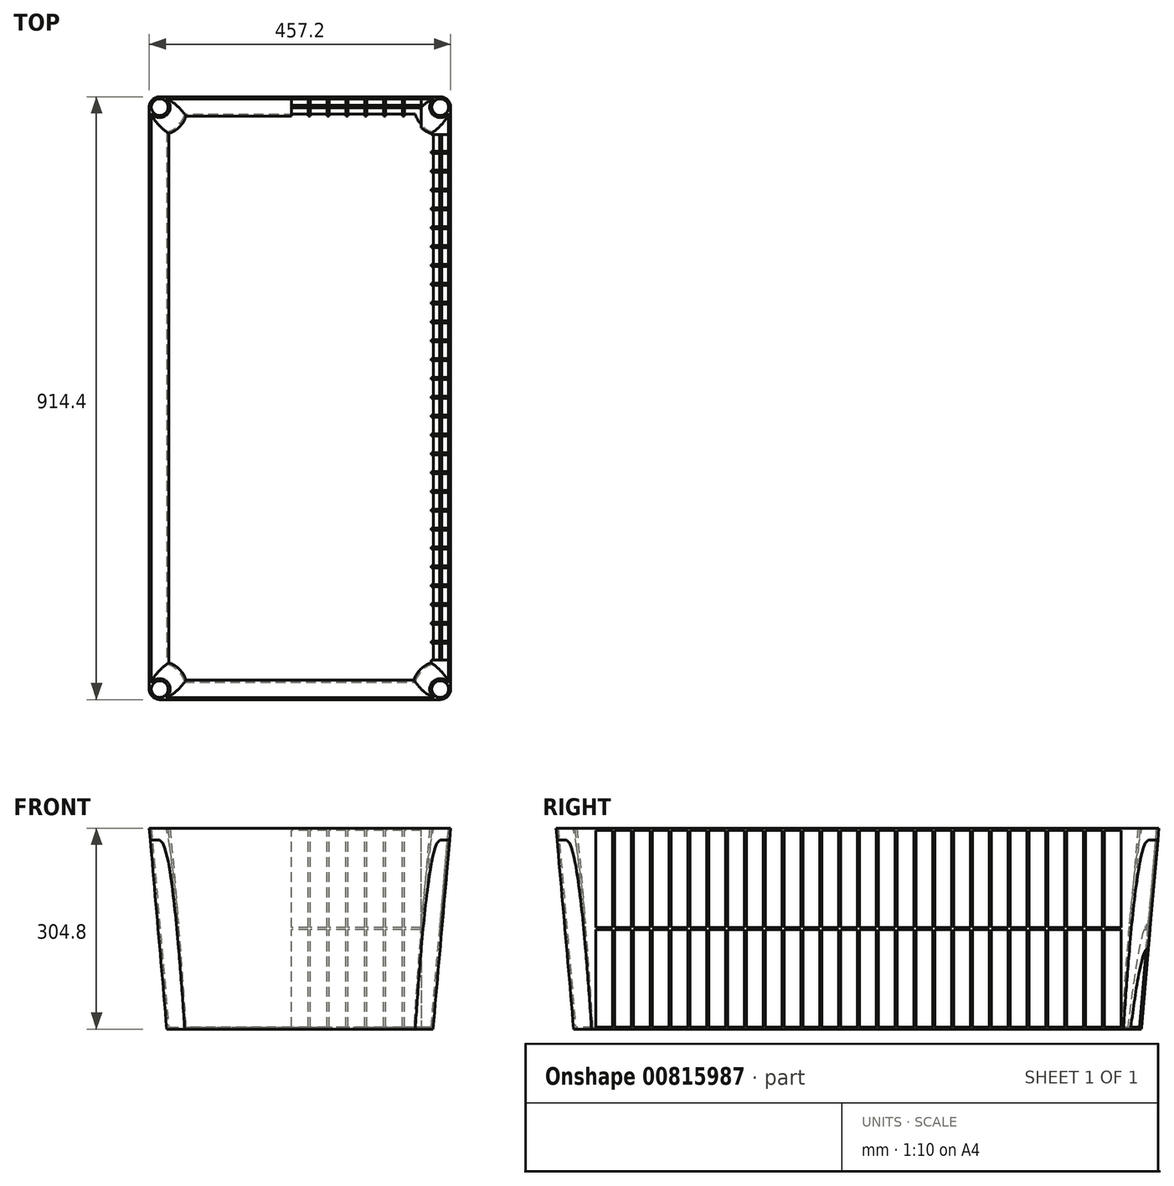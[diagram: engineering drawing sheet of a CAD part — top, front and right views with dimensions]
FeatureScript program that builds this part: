
annotation { "Feature Type Name" : "Feature", "Feature Type Description" : "" }
export const myFeature = defineFeature(function(context is Context, id is Id, definition is map)
    precondition{}
    {
        {
            var Q0;
            Q0=qCreatedBy(makeId("Right.planeOp"),FACE);
            cPlane(context, id + "F0", {"entities" : qUnion([Q0]), "cplaneType" : CPlaneType.OFFSET, "offset" : 0 * mm, "width" : 152.4 * mm, "height" : 152.4 * mm});
        }
        {
            var Q0;
            Q0=qCreatedBy(makeId("Top.planeOp"),FACE);
            var sketch = newSketch(context, id + "F1", { "sketchPlane" : qUnion([Q0])});
            skLineSegment(sketch, "E0.bottom", {"start": v(-212.73, 457.2) * mm, "end": v(212.72, 457.2) * mm});
            skLineSegment(sketch, "E0.top", {"start": v(-212.73, -457.2) * mm, "end": v(212.73, -457.2) * mm});
            skLineSegment(sketch, "E0.left", {"start": v(-228.6, 441.32) * mm, "end": v(-228.6, -441.33) * mm});
            skLineSegment(sketch, "E0.right", {"start": v(228.6, 441.33) * mm, "end": v(228.6, -441.33) * mm});
            skLineSegment(sketch, "E1", {"start": v(-228.6, 457.2) * mm, "end": v(228.6, -457.2) * mm, "construction": true});
            skPoint(sketch, "E2.visualSharp", {"position": v(-228.6, -457.2) * mm});
            skArc(sketch, "E2.filletArc", {"start": v(-228.6, -441.33) * mm, "mid": v(-223.95, -452.55) * mm, "end": v(-212.73, -457.2) * mm});
            skPoint(sketch, "E3.visualSharp", {"position": v(-228.6, 457.2) * mm});
            skArc(sketch, "E3.filletArc", {"start": v(-212.73, 457.2) * mm, "mid": v(-223.95, 452.55) * mm, "end": v(-228.6, 441.32) * mm});
            skPoint(sketch, "E4.visualSharp", {"position": v(228.6, 457.2) * mm});
            skArc(sketch, "E4.filletArc", {"start": v(228.6, 441.33) * mm, "mid": v(223.95, 452.55) * mm, "end": v(212.72, 457.2) * mm});
            skPoint(sketch, "E5.visualSharp", {"position": v(228.6, -457.2) * mm});
            skArc(sketch, "E5.filletArc", {"start": v(212.73, -457.2) * mm, "mid": v(223.95, -452.55) * mm, "end": v(228.6, -441.33) * mm});
            skCircle(sketch, "E6", {"center": v(-212.73, -441.33) * mm, "radius": 12.7 * mm});
            skCircle(sketch, "E7", {"center": v(212.73, -441.33) * mm, "radius": 12.7 * mm});
            skCircle(sketch, "E8", {"center": v(-212.73, 441.32) * mm, "radius": 12.7 * mm});
            skCircle(sketch, "E9", {"center": v(212.72, 441.33) * mm, "radius": 12.7 * mm});
            skSolve(sketch);
        }
        {
            var Q0;
            Q0=makeQuery(id+"F1.imprint","IMPRINT",FACE,{"disambiguationData":[TD([[makeQuery(id+"F1.imprint","IMPRINT",EDGE,{"derivedFrom":sQuery(id+"F1.wireOp",EDGE,"E0.bottom")}),-1.0]])]});
            extrude(context, id + "F2", {"entities" : qUnion([Q0]), "oppositeDirection" : true, "depth" : 304.8 * mm, "offsetDistance" : 25.4 * mm, "hasDraft" : true, "draftAngle" : 5 * degree, "draftPullDirection" : true});
        }
        {
            var Q0;
            Q0=makeQuery(id+"F2.opExtrude","CAP_FACE",FACE,{"disambiguationData":[OSD([sQuery(id+"F1.wireOp",EDGE,"E0.bottom"),sQuery(id+"F1.wireOp",EDGE,"E0.top"),sQuery(id+"F1.wireOp",EDGE,"E0.left"),sQuery(id+"F1.wireOp",EDGE,"E0.right"),sQuery(id+"F1.wireOp",EDGE,"E2.filletArc"),sQuery(id+"F1.wireOp",EDGE,"E3.filletArc"),sQuery(id+"F1.wireOp",EDGE,"E4.filletArc"),sQuery(id+"F1.wireOp",EDGE,"E5.filletArc"),sQuery(id+"F1.wireOp",EDGE,"E6"),sQuery(id+"F1.wireOp",EDGE,"E7"),sQuery(id+"F1.wireOp",EDGE,"E8"),sQuery(id+"F1.wireOp",EDGE,"E9")])],"isStart":true});
            shell(context, id + "F3", {"entities" : qUnion([Q0]), "thickness" : 3.17 * mm});
        }
        {
            var Q0;
            Q0=qCreatedBy(id+"F0.planeOp",FACE);
            var sketch = newSketch(context, id + "F4", { "sketchPlane" : qUnion([Q0])});
            skLineSegment(sketch, "E10.bottom", {"start": v(-396.88, -3.18) * mm, "end": v(-371.48, -3.18) * mm});
            skLineSegment(sketch, "E10.top", {"start": v(-396.88, -150.81) * mm, "end": v(-371.48, -150.81) * mm});
            skLineSegment(sketch, "E10.left", {"start": v(-396.88, -3.17) * mm, "end": v(-396.88, -150.81) * mm});
            skLineSegment(sketch, "E10.right", {"start": v(-371.48, -3.18) * mm, "end": v(-371.48, -150.81) * mm});
            skLineSegment(sketch, "E11.0.1.0", {"start": v(-371.48, -153.99) * mm, "end": v(-371.48, -301.62) * mm});
            skLineSegment(sketch, "E11.0.1.1", {"start": v(-396.88, -153.99) * mm, "end": v(-396.88, -301.63) * mm});
            skLineSegment(sketch, "E11.0.1.2", {"start": v(-396.88, -153.99) * mm, "end": v(-371.48, -153.99) * mm});
            skLineSegment(sketch, "E11.0.1.3", {"start": v(-396.88, -301.62) * mm, "end": v(-371.48, -301.62) * mm});
            skLineSegment(sketch, "E11.1.0.0", {"start": v(-342.9, -3.18) * mm, "end": v(-342.9, -150.81) * mm});
            skLineSegment(sketch, "E11.1.0.1", {"start": v(-368.3, -3.17) * mm, "end": v(-368.3, -150.81) * mm});
            skLineSegment(sketch, "E11.1.0.2", {"start": v(-368.3, -3.18) * mm, "end": v(-342.9, -3.18) * mm});
            skLineSegment(sketch, "E11.1.0.3", {"start": v(-368.3, -150.81) * mm, "end": v(-342.9, -150.81) * mm});
            skLineSegment(sketch, "E11.1.1.0", {"start": v(-342.9, -153.99) * mm, "end": v(-342.9, -301.62) * mm});
            skLineSegment(sketch, "E11.1.1.1", {"start": v(-368.3, -153.99) * mm, "end": v(-368.3, -301.63) * mm});
            skLineSegment(sketch, "E11.1.1.2", {"start": v(-368.3, -153.99) * mm, "end": v(-342.9, -153.99) * mm});
            skLineSegment(sketch, "E11.1.1.3", {"start": v(-368.3, -301.63) * mm, "end": v(-342.9, -301.63) * mm});
            skLineSegment(sketch, "E11.2.0.0", {"start": v(-314.33, -3.18) * mm, "end": v(-314.33, -150.81) * mm});
            skLineSegment(sketch, "E11.2.0.1", {"start": v(-339.73, -3.17) * mm, "end": v(-339.73, -150.81) * mm});
            skLineSegment(sketch, "E11.2.0.2", {"start": v(-339.73, -3.18) * mm, "end": v(-314.33, -3.18) * mm});
            skLineSegment(sketch, "E11.2.0.3", {"start": v(-339.72, -150.81) * mm, "end": v(-314.32, -150.81) * mm});
            skLineSegment(sketch, "E11.2.1.0", {"start": v(-314.33, -153.99) * mm, "end": v(-314.33, -301.62) * mm});
            skLineSegment(sketch, "E11.2.1.1", {"start": v(-339.73, -153.99) * mm, "end": v(-339.73, -301.63) * mm});
            skLineSegment(sketch, "E11.2.1.2", {"start": v(-339.73, -153.99) * mm, "end": v(-314.33, -153.99) * mm});
            skLineSegment(sketch, "E11.2.1.3", {"start": v(-339.72, -301.63) * mm, "end": v(-314.32, -301.63) * mm});
            skLineSegment(sketch, "E11.3.0.0", {"start": v(-285.75, -3.18) * mm, "end": v(-285.75, -150.81) * mm});
            skLineSegment(sketch, "E11.3.0.1", {"start": v(-311.15, -3.17) * mm, "end": v(-311.15, -150.81) * mm});
            skLineSegment(sketch, "E11.3.0.2", {"start": v(-311.15, -3.18) * mm, "end": v(-285.75, -3.18) * mm});
            skLineSegment(sketch, "E11.3.0.3", {"start": v(-311.15, -150.81) * mm, "end": v(-285.75, -150.81) * mm});
            skLineSegment(sketch, "E11.3.1.0", {"start": v(-285.75, -153.99) * mm, "end": v(-285.75, -301.62) * mm});
            skLineSegment(sketch, "E11.3.1.1", {"start": v(-311.15, -153.99) * mm, "end": v(-311.15, -301.63) * mm});
            skLineSegment(sketch, "E11.3.1.2", {"start": v(-311.15, -153.99) * mm, "end": v(-285.75, -153.99) * mm});
            skLineSegment(sketch, "E11.3.1.3", {"start": v(-311.15, -301.63) * mm, "end": v(-285.75, -301.63) * mm});
            skLineSegment(sketch, "E11.4.0.0", {"start": v(-257.18, -3.18) * mm, "end": v(-257.18, -150.81) * mm});
            skLineSegment(sketch, "E11.4.0.1", {"start": v(-282.57, -3.17) * mm, "end": v(-282.57, -150.81) * mm});
            skLineSegment(sketch, "E11.4.0.2", {"start": v(-282.57, -3.18) * mm, "end": v(-257.18, -3.18) * mm});
            skLineSegment(sketch, "E11.4.0.3", {"start": v(-282.57, -150.81) * mm, "end": v(-257.17, -150.81) * mm});
            skLineSegment(sketch, "E11.4.1.0", {"start": v(-257.18, -153.99) * mm, "end": v(-257.18, -301.62) * mm});
            skLineSegment(sketch, "E11.4.1.1", {"start": v(-282.57, -153.99) * mm, "end": v(-282.57, -301.63) * mm});
            skLineSegment(sketch, "E11.4.1.2", {"start": v(-282.57, -153.99) * mm, "end": v(-257.18, -153.99) * mm});
            skLineSegment(sketch, "E11.4.1.3", {"start": v(-282.57, -301.63) * mm, "end": v(-257.17, -301.63) * mm});
            skLineSegment(sketch, "E11.5.0.0", {"start": v(-228.6, -3.18) * mm, "end": v(-228.6, -150.81) * mm});
            skLineSegment(sketch, "E11.5.0.1", {"start": v(-254, -3.17) * mm, "end": v(-254, -150.81) * mm});
            skLineSegment(sketch, "E11.5.0.2", {"start": v(-254, -3.18) * mm, "end": v(-228.6, -3.18) * mm});
            skLineSegment(sketch, "E11.5.0.3", {"start": v(-254, -150.81) * mm, "end": v(-228.6, -150.81) * mm});
            skLineSegment(sketch, "E11.5.1.0", {"start": v(-228.6, -153.99) * mm, "end": v(-228.6, -301.62) * mm});
            skLineSegment(sketch, "E11.5.1.1", {"start": v(-254, -153.99) * mm, "end": v(-254, -301.63) * mm});
            skLineSegment(sketch, "E11.5.1.2", {"start": v(-254, -153.99) * mm, "end": v(-228.6, -153.99) * mm});
            skLineSegment(sketch, "E11.5.1.3", {"start": v(-254, -301.63) * mm, "end": v(-228.6, -301.63) * mm});
            skLineSegment(sketch, "E11.6.0.0", {"start": v(-200.02, -3.18) * mm, "end": v(-200.02, -150.81) * mm});
            skLineSegment(sketch, "E11.6.0.1", {"start": v(-225.42, -3.17) * mm, "end": v(-225.42, -150.81) * mm});
            skLineSegment(sketch, "E11.6.0.2", {"start": v(-225.42, -3.18) * mm, "end": v(-200.02, -3.18) * mm});
            skLineSegment(sketch, "E11.6.0.3", {"start": v(-225.42, -150.81) * mm, "end": v(-200.02, -150.81) * mm});
            skLineSegment(sketch, "E11.6.1.0", {"start": v(-200.02, -153.99) * mm, "end": v(-200.02, -301.62) * mm});
            skLineSegment(sketch, "E11.6.1.1", {"start": v(-225.42, -153.99) * mm, "end": v(-225.42, -301.63) * mm});
            skLineSegment(sketch, "E11.6.1.2", {"start": v(-225.42, -153.99) * mm, "end": v(-200.02, -153.99) * mm});
            skLineSegment(sketch, "E11.6.1.3", {"start": v(-225.42, -301.63) * mm, "end": v(-200.02, -301.63) * mm});
            skLineSegment(sketch, "E11.7.0.0", {"start": v(-171.45, -3.18) * mm, "end": v(-171.45, -150.81) * mm});
            skLineSegment(sketch, "E11.7.0.1", {"start": v(-196.85, -3.17) * mm, "end": v(-196.85, -150.81) * mm});
            skLineSegment(sketch, "E11.7.0.2", {"start": v(-196.85, -3.18) * mm, "end": v(-171.45, -3.18) * mm});
            skLineSegment(sketch, "E11.7.0.3", {"start": v(-196.85, -150.81) * mm, "end": v(-171.45, -150.81) * mm});
            skLineSegment(sketch, "E11.7.1.0", {"start": v(-171.45, -153.99) * mm, "end": v(-171.45, -301.62) * mm});
            skLineSegment(sketch, "E11.7.1.1", {"start": v(-196.85, -153.99) * mm, "end": v(-196.85, -301.63) * mm});
            skLineSegment(sketch, "E11.7.1.2", {"start": v(-196.85, -153.99) * mm, "end": v(-171.45, -153.99) * mm});
            skLineSegment(sketch, "E11.7.1.3", {"start": v(-196.85, -301.63) * mm, "end": v(-171.45, -301.63) * mm});
            skLineSegment(sketch, "E11.8.0.0", {"start": v(-142.87, -3.18) * mm, "end": v(-142.87, -150.81) * mm});
            skLineSegment(sketch, "E11.8.0.1", {"start": v(-168.27, -3.17) * mm, "end": v(-168.27, -150.81) * mm});
            skLineSegment(sketch, "E11.8.0.2", {"start": v(-168.27, -3.18) * mm, "end": v(-142.87, -3.18) * mm});
            skLineSegment(sketch, "E11.8.0.3", {"start": v(-168.27, -150.81) * mm, "end": v(-142.87, -150.81) * mm});
            skLineSegment(sketch, "E11.8.1.0", {"start": v(-142.87, -153.99) * mm, "end": v(-142.87, -301.62) * mm});
            skLineSegment(sketch, "E11.8.1.1", {"start": v(-168.27, -153.99) * mm, "end": v(-168.27, -301.63) * mm});
            skLineSegment(sketch, "E11.8.1.2", {"start": v(-168.27, -153.99) * mm, "end": v(-142.87, -153.99) * mm});
            skLineSegment(sketch, "E11.8.1.3", {"start": v(-168.27, -301.63) * mm, "end": v(-142.87, -301.63) * mm});
            skLineSegment(sketch, "E11.9.0.0", {"start": v(-114.3, -3.18) * mm, "end": v(-114.3, -150.81) * mm});
            skLineSegment(sketch, "E11.9.0.1", {"start": v(-139.7, -3.17) * mm, "end": v(-139.7, -150.81) * mm});
            skLineSegment(sketch, "E11.9.0.2", {"start": v(-139.7, -3.18) * mm, "end": v(-114.3, -3.18) * mm});
            skLineSegment(sketch, "E11.9.0.3", {"start": v(-139.7, -150.81) * mm, "end": v(-114.3, -150.81) * mm});
            skLineSegment(sketch, "E11.9.1.0", {"start": v(-114.3, -153.99) * mm, "end": v(-114.3, -301.62) * mm});
            skLineSegment(sketch, "E11.9.1.1", {"start": v(-139.7, -153.99) * mm, "end": v(-139.7, -301.63) * mm});
            skLineSegment(sketch, "E11.9.1.2", {"start": v(-139.7, -153.99) * mm, "end": v(-114.3, -153.99) * mm});
            skLineSegment(sketch, "E11.9.1.3", {"start": v(-139.7, -301.63) * mm, "end": v(-114.3, -301.63) * mm});
            skLineSegment(sketch, "E11.10.0.0", {"start": v(-85.72, -3.18) * mm, "end": v(-85.72, -150.81) * mm});
            skLineSegment(sketch, "E11.10.0.1", {"start": v(-111.12, -3.17) * mm, "end": v(-111.12, -150.81) * mm});
            skLineSegment(sketch, "E11.10.0.2", {"start": v(-111.12, -3.18) * mm, "end": v(-85.72, -3.18) * mm});
            skLineSegment(sketch, "E11.10.0.3", {"start": v(-111.12, -150.81) * mm, "end": v(-85.72, -150.81) * mm});
            skLineSegment(sketch, "E11.10.1.0", {"start": v(-85.72, -153.99) * mm, "end": v(-85.72, -301.62) * mm});
            skLineSegment(sketch, "E11.10.1.1", {"start": v(-111.12, -153.99) * mm, "end": v(-111.12, -301.63) * mm});
            skLineSegment(sketch, "E11.10.1.2", {"start": v(-111.12, -153.99) * mm, "end": v(-85.72, -153.99) * mm});
            skLineSegment(sketch, "E11.10.1.3", {"start": v(-111.12, -301.63) * mm, "end": v(-85.72, -301.63) * mm});
            skLineSegment(sketch, "E11.11.0.0", {"start": v(-57.15, -3.18) * mm, "end": v(-57.15, -150.81) * mm});
            skLineSegment(sketch, "E11.11.0.1", {"start": v(-82.55, -3.17) * mm, "end": v(-82.55, -150.81) * mm});
            skLineSegment(sketch, "E11.11.0.2", {"start": v(-82.55, -3.18) * mm, "end": v(-57.15, -3.18) * mm});
            skLineSegment(sketch, "E11.11.0.3", {"start": v(-82.55, -150.81) * mm, "end": v(-57.15, -150.81) * mm});
            skLineSegment(sketch, "E11.11.1.0", {"start": v(-57.15, -153.99) * mm, "end": v(-57.15, -301.62) * mm});
            skLineSegment(sketch, "E11.11.1.1", {"start": v(-82.55, -153.99) * mm, "end": v(-82.55, -301.63) * mm});
            skLineSegment(sketch, "E11.11.1.2", {"start": v(-82.55, -153.99) * mm, "end": v(-57.15, -153.99) * mm});
            skLineSegment(sketch, "E11.11.1.3", {"start": v(-82.55, -301.63) * mm, "end": v(-57.15, -301.63) * mm});
            skLineSegment(sketch, "E11.12.0.0", {"start": v(-28.57, -3.18) * mm, "end": v(-28.57, -150.81) * mm});
            skLineSegment(sketch, "E11.12.0.1", {"start": v(-53.97, -3.17) * mm, "end": v(-53.97, -150.81) * mm});
            skLineSegment(sketch, "E11.12.0.2", {"start": v(-53.97, -3.18) * mm, "end": v(-28.57, -3.18) * mm});
            skLineSegment(sketch, "E11.12.0.3", {"start": v(-53.97, -150.81) * mm, "end": v(-28.57, -150.81) * mm});
            skLineSegment(sketch, "E11.12.1.0", {"start": v(-28.57, -153.99) * mm, "end": v(-28.57, -301.62) * mm});
            skLineSegment(sketch, "E11.12.1.1", {"start": v(-53.97, -153.99) * mm, "end": v(-53.97, -301.63) * mm});
            skLineSegment(sketch, "E11.12.1.2", {"start": v(-53.97, -153.99) * mm, "end": v(-28.57, -153.99) * mm});
            skLineSegment(sketch, "E11.12.1.3", {"start": v(-53.97, -301.63) * mm, "end": v(-28.57, -301.63) * mm});
            skLineSegment(sketch, "E11.13.0.0", {"start": v(0, -3.18) * mm, "end": v(0, -150.81) * mm});
            skLineSegment(sketch, "E11.13.0.1", {"start": v(-25.4, -3.17) * mm, "end": v(-25.4, -150.81) * mm});
            skLineSegment(sketch, "E11.13.0.2", {"start": v(-25.4, -3.18) * mm, "end": v(0, -3.18) * mm});
            skLineSegment(sketch, "E11.13.0.3", {"start": v(-25.4, -150.81) * mm, "end": v(0, -150.81) * mm});
            skLineSegment(sketch, "E11.13.1.0", {"start": v(0, -153.99) * mm, "end": v(0, -301.62) * mm});
            skLineSegment(sketch, "E11.13.1.1", {"start": v(-25.4, -153.99) * mm, "end": v(-25.4, -301.63) * mm});
            skLineSegment(sketch, "E11.13.1.2", {"start": v(-25.4, -153.99) * mm, "end": v(0, -153.99) * mm});
            skLineSegment(sketch, "E11.13.1.3", {"start": v(-25.4, -301.63) * mm, "end": v(0, -301.63) * mm});
            skLineSegment(sketch, "E11.14.0.0", {"start": v(28.58, -3.18) * mm, "end": v(28.58, -150.81) * mm});
            skLineSegment(sketch, "E11.14.0.1", {"start": v(3.18, -3.17) * mm, "end": v(3.18, -150.81) * mm});
            skLineSegment(sketch, "E11.14.0.2", {"start": v(3.18, -3.18) * mm, "end": v(28.58, -3.18) * mm});
            skLineSegment(sketch, "E11.14.0.3", {"start": v(3.18, -150.81) * mm, "end": v(28.58, -150.81) * mm});
            skLineSegment(sketch, "E11.14.1.0", {"start": v(28.58, -153.99) * mm, "end": v(28.58, -301.62) * mm});
            skLineSegment(sketch, "E11.14.1.1", {"start": v(3.18, -153.99) * mm, "end": v(3.18, -301.63) * mm});
            skLineSegment(sketch, "E11.14.1.2", {"start": v(3.18, -153.99) * mm, "end": v(28.58, -153.99) * mm});
            skLineSegment(sketch, "E11.14.1.3", {"start": v(3.18, -301.63) * mm, "end": v(28.58, -301.63) * mm});
            skLineSegment(sketch, "E11.15.0.0", {"start": v(57.15, -3.18) * mm, "end": v(57.15, -150.81) * mm});
            skLineSegment(sketch, "E11.15.0.1", {"start": v(31.75, -3.17) * mm, "end": v(31.75, -150.81) * mm});
            skLineSegment(sketch, "E11.15.0.2", {"start": v(31.75, -3.18) * mm, "end": v(57.15, -3.18) * mm});
            skLineSegment(sketch, "E11.15.0.3", {"start": v(31.75, -150.81) * mm, "end": v(57.15, -150.81) * mm});
            skLineSegment(sketch, "E11.15.1.0", {"start": v(57.15, -153.99) * mm, "end": v(57.15, -301.62) * mm});
            skLineSegment(sketch, "E11.15.1.1", {"start": v(31.75, -153.99) * mm, "end": v(31.75, -301.63) * mm});
            skLineSegment(sketch, "E11.15.1.2", {"start": v(31.75, -153.99) * mm, "end": v(57.15, -153.99) * mm});
            skLineSegment(sketch, "E11.15.1.3", {"start": v(31.75, -301.63) * mm, "end": v(57.15, -301.63) * mm});
            skLineSegment(sketch, "E11.16.0.0", {"start": v(85.73, -3.18) * mm, "end": v(85.73, -150.81) * mm});
            skLineSegment(sketch, "E11.16.0.1", {"start": v(60.33, -3.17) * mm, "end": v(60.33, -150.81) * mm});
            skLineSegment(sketch, "E11.16.0.2", {"start": v(60.33, -3.18) * mm, "end": v(85.73, -3.18) * mm});
            skLineSegment(sketch, "E11.16.0.3", {"start": v(60.33, -150.81) * mm, "end": v(85.73, -150.81) * mm});
            skLineSegment(sketch, "E11.16.1.0", {"start": v(85.73, -153.99) * mm, "end": v(85.73, -301.62) * mm});
            skLineSegment(sketch, "E11.16.1.1", {"start": v(60.33, -153.99) * mm, "end": v(60.33, -301.63) * mm});
            skLineSegment(sketch, "E11.16.1.2", {"start": v(60.33, -153.99) * mm, "end": v(85.73, -153.99) * mm});
            skLineSegment(sketch, "E11.16.1.3", {"start": v(60.33, -301.63) * mm, "end": v(85.73, -301.63) * mm});
            skLineSegment(sketch, "E11.17.0.0", {"start": v(114.3, -3.18) * mm, "end": v(114.3, -150.81) * mm});
            skLineSegment(sketch, "E11.17.0.1", {"start": v(88.9, -3.17) * mm, "end": v(88.9, -150.81) * mm});
            skLineSegment(sketch, "E11.17.0.2", {"start": v(88.9, -3.18) * mm, "end": v(114.3, -3.18) * mm});
            skLineSegment(sketch, "E11.17.0.3", {"start": v(88.9, -150.81) * mm, "end": v(114.3, -150.81) * mm});
            skLineSegment(sketch, "E11.17.1.0", {"start": v(114.3, -153.99) * mm, "end": v(114.3, -301.62) * mm});
            skLineSegment(sketch, "E11.17.1.1", {"start": v(88.9, -153.99) * mm, "end": v(88.9, -301.63) * mm});
            skLineSegment(sketch, "E11.17.1.2", {"start": v(88.9, -153.99) * mm, "end": v(114.3, -153.99) * mm});
            skLineSegment(sketch, "E11.17.1.3", {"start": v(88.9, -301.63) * mm, "end": v(114.3, -301.63) * mm});
            skLineSegment(sketch, "E11.18.0.0", {"start": v(142.88, -3.18) * mm, "end": v(142.88, -150.81) * mm});
            skLineSegment(sketch, "E11.18.0.1", {"start": v(117.48, -3.17) * mm, "end": v(117.48, -150.81) * mm});
            skLineSegment(sketch, "E11.18.0.2", {"start": v(117.48, -3.18) * mm, "end": v(142.88, -3.18) * mm});
            skLineSegment(sketch, "E11.18.0.3", {"start": v(117.48, -150.81) * mm, "end": v(142.88, -150.81) * mm});
            skLineSegment(sketch, "E11.18.1.0", {"start": v(142.88, -153.99) * mm, "end": v(142.88, -301.62) * mm});
            skLineSegment(sketch, "E11.18.1.1", {"start": v(117.48, -153.99) * mm, "end": v(117.48, -301.63) * mm});
            skLineSegment(sketch, "E11.18.1.2", {"start": v(117.48, -153.99) * mm, "end": v(142.88, -153.99) * mm});
            skLineSegment(sketch, "E11.18.1.3", {"start": v(117.48, -301.63) * mm, "end": v(142.88, -301.63) * mm});
            skLineSegment(sketch, "E11.19.0.0", {"start": v(171.45, -3.18) * mm, "end": v(171.45, -150.81) * mm});
            skLineSegment(sketch, "E11.19.0.1", {"start": v(146.05, -3.17) * mm, "end": v(146.05, -150.81) * mm});
            skLineSegment(sketch, "E11.19.0.2", {"start": v(146.05, -3.18) * mm, "end": v(171.45, -3.18) * mm});
            skLineSegment(sketch, "E11.19.0.3", {"start": v(146.05, -150.81) * mm, "end": v(171.45, -150.81) * mm});
            skLineSegment(sketch, "E11.19.1.0", {"start": v(171.45, -153.99) * mm, "end": v(171.45, -301.62) * mm});
            skLineSegment(sketch, "E11.19.1.1", {"start": v(146.05, -153.99) * mm, "end": v(146.05, -301.63) * mm});
            skLineSegment(sketch, "E11.19.1.2", {"start": v(146.05, -153.99) * mm, "end": v(171.45, -153.99) * mm});
            skLineSegment(sketch, "E11.19.1.3", {"start": v(146.05, -301.63) * mm, "end": v(171.45, -301.63) * mm});
            skLineSegment(sketch, "E11.20.0.0", {"start": v(200.03, -3.18) * mm, "end": v(200.03, -150.81) * mm});
            skLineSegment(sketch, "E11.20.0.1", {"start": v(174.63, -3.17) * mm, "end": v(174.63, -150.81) * mm});
            skLineSegment(sketch, "E11.20.0.2", {"start": v(174.63, -3.18) * mm, "end": v(200.03, -3.18) * mm});
            skLineSegment(sketch, "E11.20.0.3", {"start": v(174.63, -150.81) * mm, "end": v(200.03, -150.81) * mm});
            skLineSegment(sketch, "E11.20.1.0", {"start": v(200.03, -153.99) * mm, "end": v(200.03, -301.62) * mm});
            skLineSegment(sketch, "E11.20.1.1", {"start": v(174.63, -153.99) * mm, "end": v(174.63, -301.63) * mm});
            skLineSegment(sketch, "E11.20.1.2", {"start": v(174.63, -153.99) * mm, "end": v(200.03, -153.99) * mm});
            skLineSegment(sketch, "E11.20.1.3", {"start": v(174.63, -301.63) * mm, "end": v(200.03, -301.63) * mm});
            skLineSegment(sketch, "E11.21.0.0", {"start": v(228.6, -3.18) * mm, "end": v(228.6, -150.81) * mm});
            skLineSegment(sketch, "E11.21.0.1", {"start": v(203.2, -3.17) * mm, "end": v(203.2, -150.81) * mm});
            skLineSegment(sketch, "E11.21.0.2", {"start": v(203.2, -3.18) * mm, "end": v(228.6, -3.18) * mm});
            skLineSegment(sketch, "E11.21.0.3", {"start": v(203.2, -150.81) * mm, "end": v(228.6, -150.81) * mm});
            skLineSegment(sketch, "E11.21.1.0", {"start": v(228.6, -153.99) * mm, "end": v(228.6, -301.62) * mm});
            skLineSegment(sketch, "E11.21.1.1", {"start": v(203.2, -153.99) * mm, "end": v(203.2, -301.63) * mm});
            skLineSegment(sketch, "E11.21.1.2", {"start": v(203.2, -153.99) * mm, "end": v(228.6, -153.99) * mm});
            skLineSegment(sketch, "E11.21.1.3", {"start": v(203.2, -301.63) * mm, "end": v(228.6, -301.63) * mm});
            skLineSegment(sketch, "E11.22.0.0", {"start": v(257.18, -3.18) * mm, "end": v(257.18, -150.81) * mm});
            skLineSegment(sketch, "E11.22.0.1", {"start": v(231.78, -3.17) * mm, "end": v(231.78, -150.81) * mm});
            skLineSegment(sketch, "E11.22.0.2", {"start": v(231.78, -3.18) * mm, "end": v(257.18, -3.18) * mm});
            skLineSegment(sketch, "E11.22.0.3", {"start": v(231.78, -150.81) * mm, "end": v(257.18, -150.81) * mm});
            skLineSegment(sketch, "E11.22.1.0", {"start": v(257.18, -153.99) * mm, "end": v(257.18, -301.62) * mm});
            skLineSegment(sketch, "E11.22.1.1", {"start": v(231.78, -153.99) * mm, "end": v(231.78, -301.63) * mm});
            skLineSegment(sketch, "E11.22.1.2", {"start": v(231.78, -153.99) * mm, "end": v(257.18, -153.99) * mm});
            skLineSegment(sketch, "E11.22.1.3", {"start": v(231.78, -301.63) * mm, "end": v(257.18, -301.63) * mm});
            skLineSegment(sketch, "E11.23.0.0", {"start": v(285.75, -3.18) * mm, "end": v(285.75, -150.81) * mm});
            skLineSegment(sketch, "E11.23.0.1", {"start": v(260.35, -3.17) * mm, "end": v(260.35, -150.81) * mm});
            skLineSegment(sketch, "E11.23.0.2", {"start": v(260.35, -3.18) * mm, "end": v(285.75, -3.18) * mm});
            skLineSegment(sketch, "E11.23.0.3", {"start": v(260.35, -150.81) * mm, "end": v(285.75, -150.81) * mm});
            skLineSegment(sketch, "E11.23.1.0", {"start": v(285.75, -153.99) * mm, "end": v(285.75, -301.62) * mm});
            skLineSegment(sketch, "E11.23.1.1", {"start": v(260.35, -153.99) * mm, "end": v(260.35, -301.63) * mm});
            skLineSegment(sketch, "E11.23.1.2", {"start": v(260.35, -153.99) * mm, "end": v(285.75, -153.99) * mm});
            skLineSegment(sketch, "E11.23.1.3", {"start": v(260.35, -301.63) * mm, "end": v(285.75, -301.63) * mm});
            skLineSegment(sketch, "E11.24.0.0", {"start": v(314.33, -3.18) * mm, "end": v(314.33, -150.81) * mm});
            skLineSegment(sketch, "E11.24.0.1", {"start": v(288.93, -3.17) * mm, "end": v(288.93, -150.81) * mm});
            skLineSegment(sketch, "E11.24.0.2", {"start": v(288.93, -3.18) * mm, "end": v(314.33, -3.18) * mm});
            skLineSegment(sketch, "E11.24.0.3", {"start": v(288.93, -150.81) * mm, "end": v(314.33, -150.81) * mm});
            skLineSegment(sketch, "E11.24.1.0", {"start": v(314.33, -153.99) * mm, "end": v(314.33, -301.62) * mm});
            skLineSegment(sketch, "E11.24.1.1", {"start": v(288.93, -153.99) * mm, "end": v(288.93, -301.63) * mm});
            skLineSegment(sketch, "E11.24.1.2", {"start": v(288.93, -153.99) * mm, "end": v(314.33, -153.99) * mm});
            skLineSegment(sketch, "E11.24.1.3", {"start": v(288.93, -301.63) * mm, "end": v(314.33, -301.63) * mm});
            skLineSegment(sketch, "E11.25.0.0", {"start": v(342.9, -3.18) * mm, "end": v(342.9, -150.81) * mm});
            skLineSegment(sketch, "E11.25.0.1", {"start": v(317.5, -3.17) * mm, "end": v(317.5, -150.81) * mm});
            skLineSegment(sketch, "E11.25.0.2", {"start": v(317.5, -3.18) * mm, "end": v(342.9, -3.18) * mm});
            skLineSegment(sketch, "E11.25.0.3", {"start": v(317.5, -150.81) * mm, "end": v(342.9, -150.81) * mm});
            skLineSegment(sketch, "E11.25.1.0", {"start": v(342.9, -153.99) * mm, "end": v(342.9, -301.62) * mm});
            skLineSegment(sketch, "E11.25.1.1", {"start": v(317.5, -153.99) * mm, "end": v(317.5, -301.63) * mm});
            skLineSegment(sketch, "E11.25.1.2", {"start": v(317.5, -153.99) * mm, "end": v(342.9, -153.99) * mm});
            skLineSegment(sketch, "E11.25.1.3", {"start": v(317.5, -301.63) * mm, "end": v(342.9, -301.63) * mm});
            skLineSegment(sketch, "E11.26.0.0", {"start": v(371.48, -3.18) * mm, "end": v(371.48, -150.81) * mm});
            skLineSegment(sketch, "E11.26.0.1", {"start": v(346.08, -3.17) * mm, "end": v(346.08, -150.81) * mm});
            skLineSegment(sketch, "E11.26.0.2", {"start": v(346.08, -3.18) * mm, "end": v(371.48, -3.18) * mm});
            skLineSegment(sketch, "E11.26.0.3", {"start": v(346.08, -150.81) * mm, "end": v(371.48, -150.81) * mm});
            skLineSegment(sketch, "E11.26.1.0", {"start": v(371.48, -153.99) * mm, "end": v(371.48, -301.62) * mm});
            skLineSegment(sketch, "E11.26.1.1", {"start": v(346.08, -153.99) * mm, "end": v(346.08, -301.63) * mm});
            skLineSegment(sketch, "E11.26.1.2", {"start": v(346.08, -153.99) * mm, "end": v(371.48, -153.99) * mm});
            skLineSegment(sketch, "E11.26.1.3", {"start": v(346.08, -301.63) * mm, "end": v(371.48, -301.63) * mm});
            skLineSegment(sketch, "E11.27.0.0", {"start": v(400.05, -3.18) * mm, "end": v(400.05, -150.81) * mm});
            skLineSegment(sketch, "E11.27.0.1", {"start": v(374.65, -3.17) * mm, "end": v(374.65, -150.81) * mm});
            skLineSegment(sketch, "E11.27.0.2", {"start": v(374.65, -3.18) * mm, "end": v(400.05, -3.18) * mm});
            skLineSegment(sketch, "E11.27.0.3", {"start": v(374.65, -150.81) * mm, "end": v(400.05, -150.81) * mm});
            skLineSegment(sketch, "E11.27.1.0", {"start": v(400.05, -153.99) * mm, "end": v(400.05, -301.62) * mm});
            skLineSegment(sketch, "E11.27.1.1", {"start": v(374.65, -153.99) * mm, "end": v(374.65, -301.62) * mm});
            skLineSegment(sketch, "E11.27.1.2", {"start": v(374.65, -153.99) * mm, "end": v(400.05, -153.99) * mm});
            skLineSegment(sketch, "E11.27.1.3", {"start": v(374.65, -301.63) * mm, "end": v(400.05, -301.63) * mm});
            skLineSegment(sketch, "E11.direction1", {"start": v(-396.88, -150.81) * mm, "end": v(-368.3, -150.81) * mm, "construction": true});
            skLineSegment(sketch, "E11.direction2", {"start": v(-396.88, -150.81) * mm, "end": v(-396.88, -301.63) * mm, "construction": true});
            skSolve(sketch);
        }
        {
            var Q0;
            Q0 = qSketchRegion(id + "F4", true);
            extrude(context, id + "F5", {"entities" : qUnion([Q0]), "operationType" : NewBodyOperationType.REMOVE, "endBound" : BoundingType.THROUGH_ALL, "depth" : 25.4 * mm, "offsetDistance" : 25.4 * mm});
        }
        {
            var Q0;
            Q0=qCreatedBy(makeId("Front.planeOp"),FACE);
            var Q1;
            Q1=qCreatedBy(makeId("Origin.pointOp"),VERTEX);
            cPlane(context, id + "F6", {"entities" : qUnion([Q0, Q1]), "cplaneType" : CPlaneType.PLANE_POINT, "offset" : 0 * mm, "width" : 152.4 * mm, "height" : 152.4 * mm});
        }
        {
            var Q0;
            Q0=qCreatedBy(id+"F6.planeOp",FACE);
            var sketch = newSketch(context, id + "F7", { "sketchPlane" : qUnion([Q0])});
            skLineSegment(sketch, "E12.bottom", {"start": v(-12.7, -3.18) * mm, "end": v(12.7, -3.18) * mm});
            skLineSegment(sketch, "E12.top", {"start": v(-12.7, -150.81) * mm, "end": v(12.7, -150.81) * mm});
            skLineSegment(sketch, "E12.left", {"start": v(-12.7, -3.18) * mm, "end": v(-12.7, -150.81) * mm});
            skLineSegment(sketch, "E12.right", {"start": v(12.7, -3.17) * mm, "end": v(12.7, -150.81) * mm});
            skLineSegment(sketch, "E13", {"start": v(0, -3.17) * mm, "end": v(0, -150.81) * mm, "construction": true});
            skLineSegment(sketch, "E14.bottom", {"start": v(-12.7, -153.99) * mm, "end": v(12.7, -153.99) * mm});
            skLineSegment(sketch, "E14.top", {"start": v(-12.7, -301.63) * mm, "end": v(12.7, -301.63) * mm});
            skLineSegment(sketch, "E14.left", {"start": v(-12.7, -153.99) * mm, "end": v(-12.7, -301.63) * mm});
            skLineSegment(sketch, "E14.right", {"start": v(12.7, -153.99) * mm, "end": v(12.7, -301.63) * mm});
            skLineSegment(sketch, "E15.1.0.0", {"start": v(15.88, -153.99) * mm, "end": v(15.88, -301.63) * mm});
            skLineSegment(sketch, "E15.1.0.1", {"start": v(28.58, -3.17) * mm, "end": v(28.58, -150.81) * mm, "construction": true});
            skLineSegment(sketch, "E15.1.0.2", {"start": v(41.27, -3.17) * mm, "end": v(41.27, -150.81) * mm});
            skLineSegment(sketch, "E15.1.0.3", {"start": v(41.27, -153.99) * mm, "end": v(41.27, -301.63) * mm});
            skLineSegment(sketch, "E15.1.0.4", {"start": v(15.88, -3.18) * mm, "end": v(15.88, -150.81) * mm});
            skLineSegment(sketch, "E15.1.0.5", {"start": v(15.87, -3.18) * mm, "end": v(41.28, -3.18) * mm});
            skLineSegment(sketch, "E15.1.0.6", {"start": v(15.88, -301.63) * mm, "end": v(41.27, -301.63) * mm});
            skLineSegment(sketch, "E15.1.0.7", {"start": v(15.88, -150.81) * mm, "end": v(41.27, -150.81) * mm});
            skLineSegment(sketch, "E15.1.0.8", {"start": v(15.88, -153.99) * mm, "end": v(41.28, -153.99) * mm});
            skLineSegment(sketch, "E15.2.0.0", {"start": v(44.45, -153.99) * mm, "end": v(44.45, -301.63) * mm});
            skLineSegment(sketch, "E15.2.0.1", {"start": v(57.15, -3.17) * mm, "end": v(57.15, -150.81) * mm, "construction": true});
            skLineSegment(sketch, "E15.2.0.2", {"start": v(69.85, -3.17) * mm, "end": v(69.85, -150.81) * mm});
            skLineSegment(sketch, "E15.2.0.3", {"start": v(69.85, -153.99) * mm, "end": v(69.85, -301.63) * mm});
            skLineSegment(sketch, "E15.2.0.4", {"start": v(44.45, -3.18) * mm, "end": v(44.45, -150.81) * mm});
            skLineSegment(sketch, "E15.2.0.5", {"start": v(44.45, -3.18) * mm, "end": v(69.85, -3.18) * mm});
            skLineSegment(sketch, "E15.2.0.6", {"start": v(44.45, -301.63) * mm, "end": v(69.85, -301.63) * mm});
            skLineSegment(sketch, "E15.2.0.7", {"start": v(44.45, -150.81) * mm, "end": v(69.85, -150.81) * mm});
            skLineSegment(sketch, "E15.2.0.8", {"start": v(44.45, -153.99) * mm, "end": v(69.85, -153.99) * mm});
            skLineSegment(sketch, "E15.3.0.0", {"start": v(73.03, -153.99) * mm, "end": v(73.03, -301.63) * mm});
            skLineSegment(sketch, "E15.3.0.1", {"start": v(85.73, -3.17) * mm, "end": v(85.73, -150.81) * mm, "construction": true});
            skLineSegment(sketch, "E15.3.0.2", {"start": v(98.43, -3.17) * mm, "end": v(98.43, -150.81) * mm});
            skLineSegment(sketch, "E15.3.0.3", {"start": v(98.42, -153.99) * mm, "end": v(98.42, -301.63) * mm});
            skLineSegment(sketch, "E15.3.0.4", {"start": v(73.03, -3.18) * mm, "end": v(73.03, -150.81) * mm});
            skLineSegment(sketch, "E15.3.0.5", {"start": v(73.02, -3.18) * mm, "end": v(98.43, -3.18) * mm});
            skLineSegment(sketch, "E15.3.0.6", {"start": v(73.03, -301.63) * mm, "end": v(98.42, -301.63) * mm});
            skLineSegment(sketch, "E15.3.0.7", {"start": v(73.03, -150.81) * mm, "end": v(98.42, -150.81) * mm});
            skLineSegment(sketch, "E15.3.0.8", {"start": v(73.03, -153.99) * mm, "end": v(98.43, -153.99) * mm});
            skLineSegment(sketch, "E15.4.0.0", {"start": v(101.6, -153.99) * mm, "end": v(101.6, -301.63) * mm});
            skLineSegment(sketch, "E15.4.0.1", {"start": v(114.3, -3.17) * mm, "end": v(114.3, -150.81) * mm, "construction": true});
            skLineSegment(sketch, "E15.4.0.2", {"start": v(127, -3.17) * mm, "end": v(127, -150.81) * mm});
            skLineSegment(sketch, "E15.4.0.3", {"start": v(127, -153.99) * mm, "end": v(127, -301.63) * mm});
            skLineSegment(sketch, "E15.4.0.4", {"start": v(101.6, -3.18) * mm, "end": v(101.6, -150.81) * mm});
            skLineSegment(sketch, "E15.4.0.5", {"start": v(101.6, -3.18) * mm, "end": v(127, -3.18) * mm});
            skLineSegment(sketch, "E15.4.0.6", {"start": v(101.6, -301.63) * mm, "end": v(127, -301.63) * mm});
            skLineSegment(sketch, "E15.4.0.7", {"start": v(101.6, -150.81) * mm, "end": v(127, -150.81) * mm});
            skLineSegment(sketch, "E15.4.0.8", {"start": v(101.6, -153.99) * mm, "end": v(127, -153.99) * mm});
            skLineSegment(sketch, "E15.5.0.0", {"start": v(130.18, -153.99) * mm, "end": v(130.18, -301.63) * mm});
            skLineSegment(sketch, "E15.5.0.1", {"start": v(142.88, -3.17) * mm, "end": v(142.88, -150.81) * mm, "construction": true});
            skLineSegment(sketch, "E15.5.0.2", {"start": v(155.58, -3.17) * mm, "end": v(155.58, -150.81) * mm});
            skLineSegment(sketch, "E15.5.0.3", {"start": v(155.58, -153.99) * mm, "end": v(155.58, -301.63) * mm});
            skLineSegment(sketch, "E15.5.0.4", {"start": v(130.18, -3.18) * mm, "end": v(130.18, -150.81) * mm});
            skLineSegment(sketch, "E15.5.0.5", {"start": v(130.18, -3.18) * mm, "end": v(155.58, -3.18) * mm});
            skLineSegment(sketch, "E15.5.0.6", {"start": v(130.18, -301.63) * mm, "end": v(155.58, -301.63) * mm});
            skLineSegment(sketch, "E15.5.0.7", {"start": v(130.18, -150.81) * mm, "end": v(155.58, -150.81) * mm});
            skLineSegment(sketch, "E15.5.0.8", {"start": v(130.18, -153.99) * mm, "end": v(155.58, -153.99) * mm});
            skLineSegment(sketch, "E15.6.0.0", {"start": v(158.75, -153.99) * mm, "end": v(158.75, -301.63) * mm});
            skLineSegment(sketch, "E15.6.0.1", {"start": v(171.45, -3.17) * mm, "end": v(171.45, -150.81) * mm, "construction": true});
            skLineSegment(sketch, "E15.6.0.2", {"start": v(184.15, -3.17) * mm, "end": v(184.15, -150.81) * mm});
            skLineSegment(sketch, "E15.6.0.3", {"start": v(184.15, -153.99) * mm, "end": v(184.15, -301.63) * mm});
            skLineSegment(sketch, "E15.6.0.4", {"start": v(158.75, -3.18) * mm, "end": v(158.75, -150.81) * mm});
            skLineSegment(sketch, "E15.6.0.5", {"start": v(158.75, -3.18) * mm, "end": v(184.15, -3.18) * mm});
            skLineSegment(sketch, "E15.6.0.6", {"start": v(158.75, -301.63) * mm, "end": v(184.15, -301.63) * mm});
            skLineSegment(sketch, "E15.6.0.7", {"start": v(158.75, -150.81) * mm, "end": v(184.15, -150.81) * mm});
            skLineSegment(sketch, "E15.6.0.8", {"start": v(158.75, -153.99) * mm, "end": v(184.15, -153.99) * mm});
            skLineSegment(sketch, "E15.direction1", {"start": v(-12.7, -301.63) * mm, "end": v(15.88, -301.63) * mm, "construction": true});
            skSolve(sketch);
        }
        {
            var Q0;
            Q0 = qSketchRegion(id + "F7", true);
            extrude(context, id + "F8", {"entities" : qUnion([Q0]), "operationType" : NewBodyOperationType.REMOVE, "endBound" : BoundingType.THROUGH_ALL, "oppositeDirection" : true, "depth" : 25.4 * mm, "offsetDistance" : 25.4 * mm});
        }
    });
